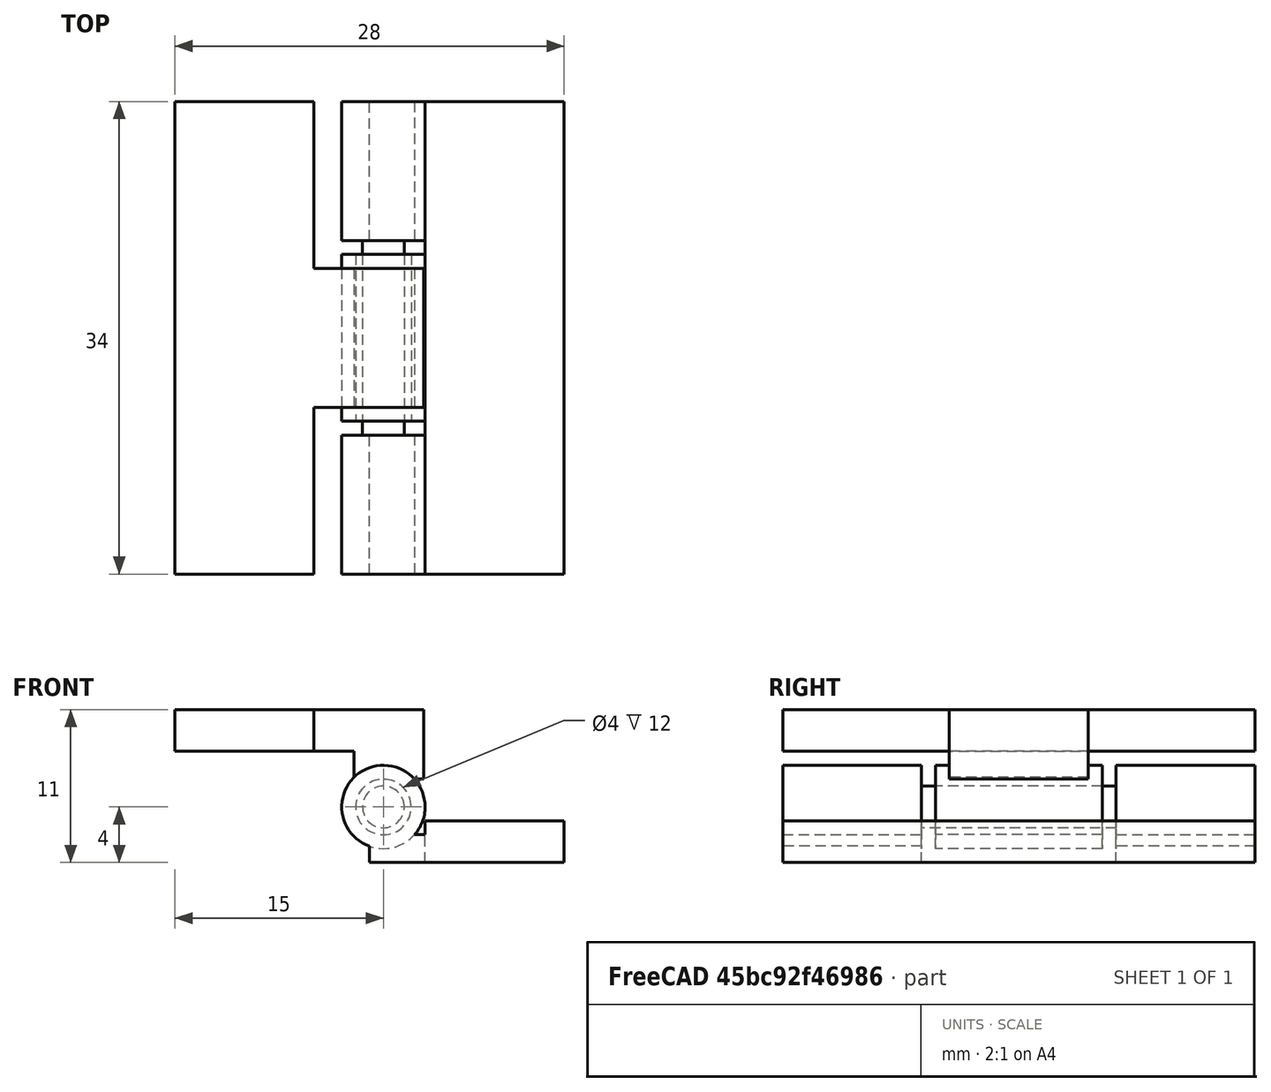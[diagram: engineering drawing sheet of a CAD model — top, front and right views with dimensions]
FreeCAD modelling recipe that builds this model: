
FCSTD DOCUMENT  (FreeCAD 0.16R6712 (Git))
Label: Hinge05
License: All rights reserved
LicenseURL: http://en.wikipedia.org/wiki/All_rights_reserved
objects: Part::Box×6, Part::Cylinder×5, Part::MultiFuse×5, Part::Cut×1
note: 17 computed .brp shape members not serialized (recipe doc carries the construction recipe); baked Part::Feature solids carry a one-line shape summary decoded from their .brp

FEATURE [Part::Cylinder] Cylinder
  Angle = 360
  Height = 10
  Placement = pos=(0,0,-2) rot=(1,0,0;1.5708rad)
  Radius = 3
FEATURE [Part::Cylinder] Cylinder001
  Angle = 360
  Height = 12
  Placement = pos=(0,13,-2) rot=(1,0,0;1.5708rad)
  Radius = 3
FEATURE [Part::Cylinder] Cylinder002
  Angle = 360
  Height = 10
  Placement = pos=(0,24,-2) rot=(1,0,0;1.5708rad)
  Radius = 3
FEATURE [Part::Cylinder] Cylinder003
  Angle = 360
  Height = 12
  Placement = pos=(0,13,-2) rot=(1,0,0;1.5708rad)
  Radius = 2
FEATURE [Part::Cut] Cut
  Base = -> Cylinder001
  Tool = -> Cylinder003
FEATURE [Part::Cylinder] Cylinder004
  Angle = 360
  Height = 30
  Placement = pos=(0,22,-2) rot=(1,0,0;1.5708rad)
  Radius = 1.5
FEATURE [Part::MultiFuse] Fusion
  Shapes = -> [Cylinder,Cylinder002,Cylinder004]
FEATURE [Part::Box] Box  label="Cube"
  Height = 3
  Length = 10
  Placement = pos=(-15,-10,2) rot=(0,0,1;0rad)
  Width = 34
FEATURE [Part::Box] Box001  label="Cube001"
  Height = 3
  Length = 10
  Placement = pos=(3,-10,-6) rot=(0,0,1;0rad)
  Width = 34
FEATURE [Part::Box] Box002  label="Cube002"
  Height = 3
  Length = 8
  Placement = pos=(-5.1,2,2) rot=(0,0,1;0rad)
  Width = 10
FEATURE [Part::MultiFuse] Fusion001
  Shapes = -> [Box,Box002]
FEATURE [Part::MultiFuse] Fusion002
  Shapes = -> [Cut,Fusion001]
FEATURE [Part::Box] Box003  label="Cube003"
  Height = 2
  Length = 4
  Placement = pos=(-1,-10,-6) rot=(0,0,1;0rad)
  Width = 10
FEATURE [Part::Box] Box004  label="Cube004"
  Height = 2
  Length = 4
  Placement = pos=(-1,14,-6) rot=(0,0,1;0rad)
  Width = 10
FEATURE [Part::MultiFuse] Fusion003
  Shapes = -> [Box004,Box003,Box001,Fusion]
FEATURE [Part::Box] Box005  label="Cube005"
  Height = 3
  Length = 5
  Placement = pos=(-2.1,2,0) rot=(0,0,1;0rad)
  Width = 10
FEATURE [Part::MultiFuse] Fusion004
  Shapes = -> [Box005,Fusion002]
